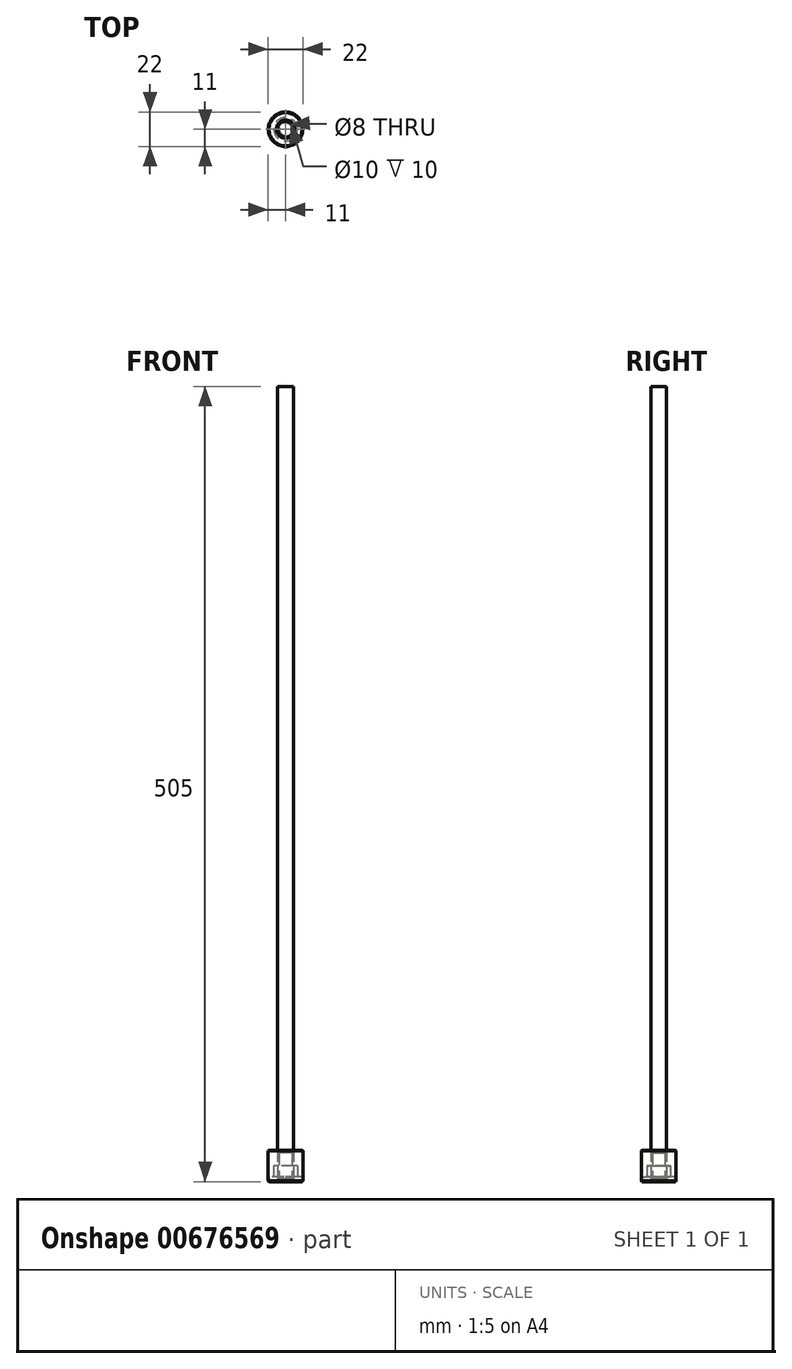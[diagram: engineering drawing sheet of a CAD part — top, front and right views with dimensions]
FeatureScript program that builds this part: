
annotation { "Feature Type Name" : "Feature", "Feature Type Description" : "" }
export const myFeature = defineFeature(function(context is Context, id is Id, definition is map)
    precondition{}
    {
        {
            var Q0;
            Q0=qCreatedBy(makeId("Top.planeOp"),FACE);
            var sketch = newSketch(context, id + "F0", { "sketchPlane" : qUnion([Q0])});
            skCircle(sketch, "E0", {"center": v(0, 0) * mm, "radius": 5 * mm});
            skCircle(sketch, "E1", {"center": v(0, 0) * mm, "radius": 7.5 * mm});
            skCircle(sketch, "E2", {"center": v(0, 0) * mm, "radius": 10.5 * mm});
            skSolve(sketch);
        }
        {
            var Q0;
            Q0=makeQuery(id+"F0.imprint","IMPRINT",FACE,{"disambiguationData":[TD([[makeQuery(id+"F0.imprint","IMPRINT",EDGE,{"derivedFrom":sQuery(id+"F0.wireOp",EDGE,"E0")}),-1.0]])]});
            extrude(context, id + "F1", {"entities" : qUnion([Q0]), "depth" : 10 * mm, "offsetDistance" : 25 * mm});
        }
        {
            var Q0;
            Q0=makeQuery(id+"F0.imprint","IMPRINT",FACE,{"disambiguationData":[TD([[makeQuery(id+"F0.imprint","IMPRINT",EDGE,{"derivedFrom":sQuery(id+"F0.wireOp",EDGE,"E1")}),-1.0]])]});
            extrude(context, id + "F2", {"entities" : qUnion([Q0]), "operationType" : NewBodyOperationType.ADD, "depth" : 3 * mm, "offsetDistance" : 25 * mm});
        }
        {
            var Q0;
            Q0=qCreatedBy(makeId("Top.planeOp"),FACE);
            var sketch = newSketch(context, id + "F3", { "sketchPlane" : qUnion([Q0])});
            skCircle(sketch, "E3", {"center": v(0, 0) * mm, "radius": 11 * mm});
            skCircle(sketch, "E4", {"center": v(0, 0) * mm, "radius": 4 * mm});
            skSolve(sketch);
        }
        {
            var Q0;
            Q0=makeQuery(id+"F3.imprint","IMPRINT",FACE,{"disambiguationData":[TD([[makeQuery(id+"F3.imprint","IMPRINT",EDGE,{"derivedFrom":sQuery(id+"F3.wireOp",EDGE,"E3")}),1.0]])]});
            extrude(context, id + "F4", {"entities" : qUnion([Q0]), "depth" : 20 * mm, "offsetDistance" : 25 * mm});
        }
        {
            var Q0;
            Q0=makeQuery(id+"F4.opExtrude","CAP_EDGE",EDGE,{"disambiguationData":[OSD([sQuery(id+"F3.wireOp",EDGE,"E4")])],"isStart":false});
            var Q1;
            Q1=makeQuery(id+"F4.opExtrude","CAP_EDGE",EDGE,{"disambiguationData":[OSD([sQuery(id+"F3.wireOp",EDGE,"E4")])],"isStart":true});
            chamfer(context, id + "F5", {"entities" : qUnion([Q0, Q1]), "width" : ((11.5 - 8) / 2) * mm, "tangentPropagation" : true});
        }
        {
            var Q0;
            Q0=makeQuery(id+"F4.opExtrude","CAP_EDGE",EDGE,{"disambiguationData":[OSD([sQuery(id+"F3.wireOp",EDGE,"E3")])],"isStart":false});
            var Q1;
            Q1=makeQuery(id+"F4.opExtrude","CAP_EDGE",EDGE,{"disambiguationData":[OSD([sQuery(id+"F3.wireOp",EDGE,"E3")])],"isStart":true});
            chamfer(context, id + "F6", {"entities" : qUnion([Q0, Q1]), "width" : .5 * mm, "tangentPropagation" : true});
        }
        {
            var Q0;
            Q0=qCreatedBy(makeId("Top.planeOp"),FACE);
            var sketch = newSketch(context, id + "F7", { "sketchPlane" : qUnion([Q0])});
            skCircle(sketch, "E5", {"center": v(0, 0) * mm, "radius": 5 * mm});
            skSolve(sketch);
        }
        {
            var Q0;
            Q0 = qSketchRegion(id + "F7", true);
            extrude(context, id + "F8", {"entities" : qUnion([Q0]), "depth" : 505 * mm, "offsetDistance" : 25 * mm});
        }
    });
